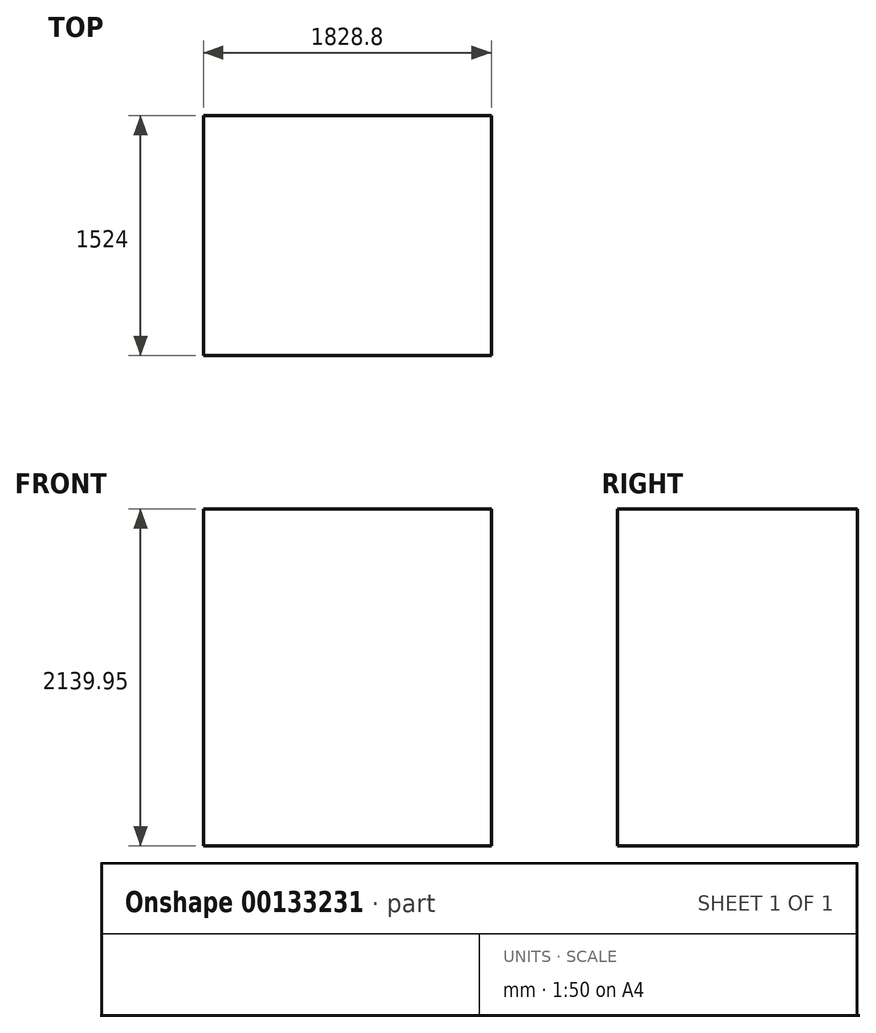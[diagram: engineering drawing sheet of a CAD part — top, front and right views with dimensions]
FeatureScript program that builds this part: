
annotation { "Feature Type Name" : "Feature", "Feature Type Description" : "" }
export const myFeature = defineFeature(function(context is Context, id is Id, definition is map)
    precondition{}
    {
        {
            var Q0;
            Q0=qCreatedBy(makeId("Front.planeOp"),FACE);
            var sketch = newSketch(context, id + "F0", { "sketchPlane" : qUnion([Q0])});
            skLineSegment(sketch, "E0.bottom", {"start": v(0, 0) * mm, "end": v(1828.8, 0) * mm});
            skLineSegment(sketch, "E0.top", {"start": v(0, 2139.95) * mm, "end": v(1828.8, 2139.95) * mm});
            skLineSegment(sketch, "E0.left", {"start": v(0, 2139.95) * mm, "end": v(0, 0) * mm});
            skLineSegment(sketch, "E0.right", {"start": v(1828.8, 2139.95) * mm, "end": v(1828.8, 0) * mm});
            skSolve(sketch);
        }
        {
            var Q0;
            Q0=makeQuery(id+"F0.imprint","IMPRINT",FACE,{"disambiguationData":[TD([[makeQuery(id+"F0.imprint","IMPRINT",EDGE,{"derivedFrom":sQuery(id+"F0.wireOp",EDGE,"E0.bottom")}),1.0]])]});
            extrude(context, id + "F1", {"entities" : qUnion([Q0]), "oppositeDirection" : true, "depth" : 1524 * mm});
        }
    });
